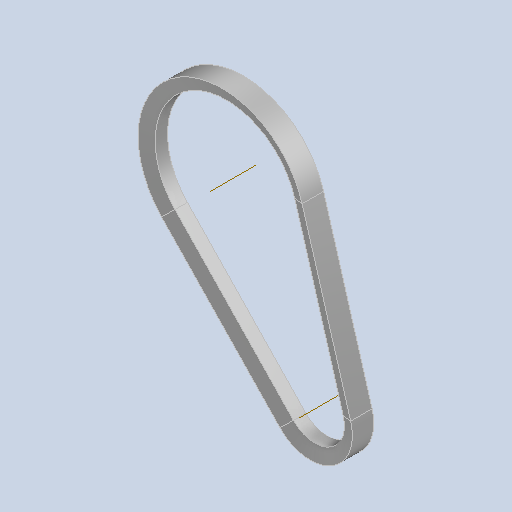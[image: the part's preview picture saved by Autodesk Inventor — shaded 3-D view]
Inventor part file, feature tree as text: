
AUTODESK INVENTOR PART (.ipt)
format: ipt  version: 2023 (Build 270158000, 158)  size: 113,152 bytes
history: native  units: mm (DEFAULTED — no unit token found)
features: other x5, sweep x1
ambient origin geometry x8: Origin, YZ Plane, XZ Plane, XY Plane, X Axis, Y Axis, Z Axis, Center Point
bodies: Solid1 (feature_tree)
feature tree (6):
  other  "Эскизная траектория"
  other  "Плоскость сечения"
  other  "РабОсь1"
  other  "РабОсь2"
  sweep  "Ремень"
  other  "Сечение"
